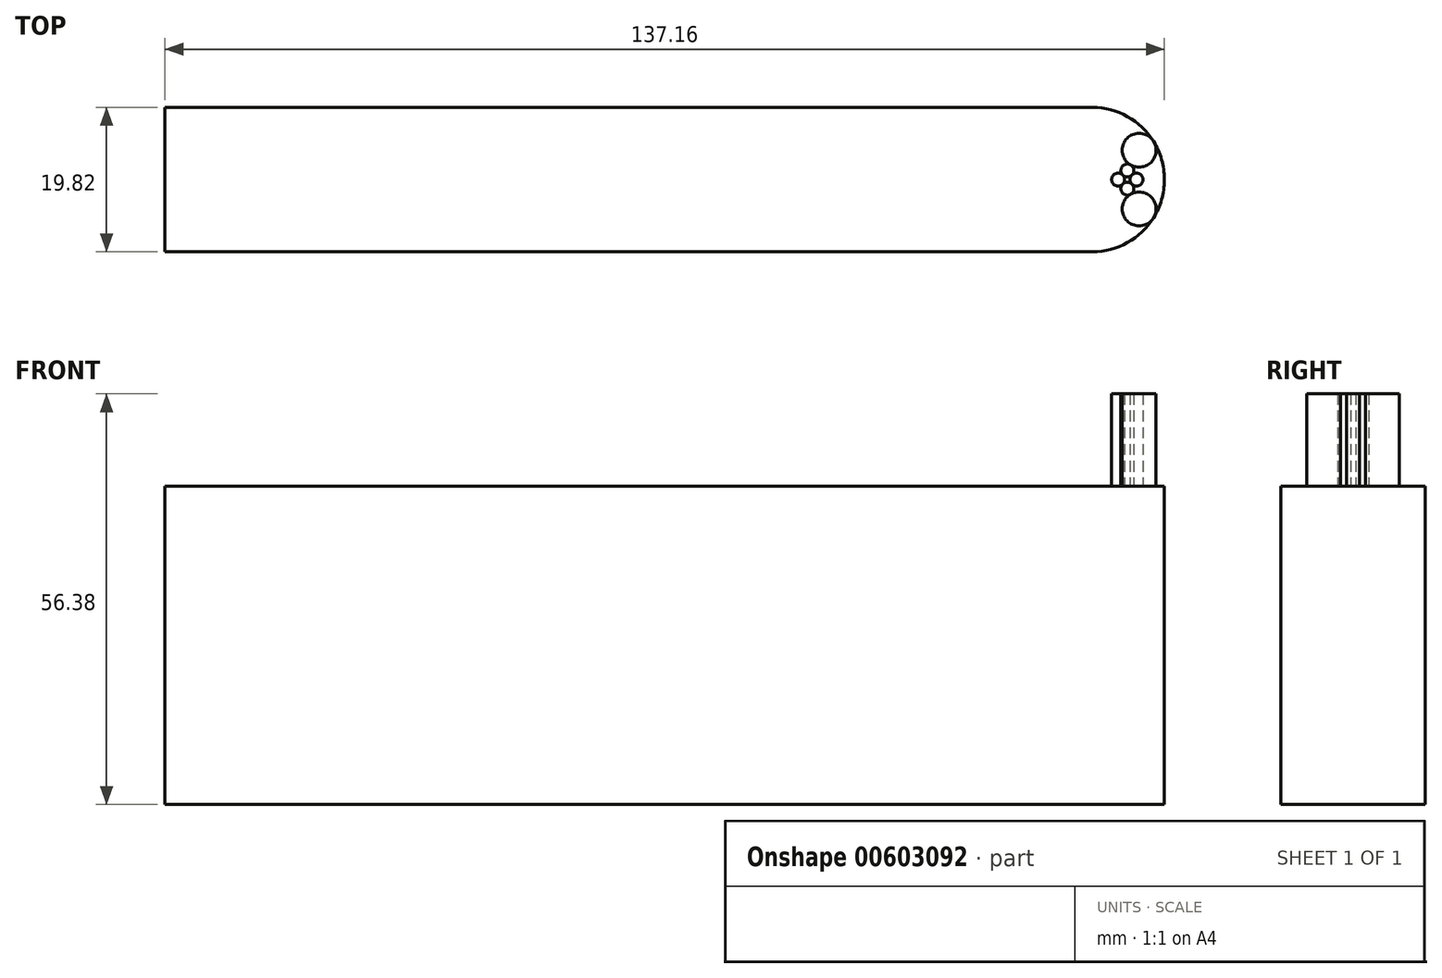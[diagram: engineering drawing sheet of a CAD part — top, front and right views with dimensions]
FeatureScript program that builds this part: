
annotation { "Feature Type Name" : "Feature", "Feature Type Description" : "" }
export const myFeature = defineFeature(function(context is Context, id is Id, definition is map)
    precondition{}
    {
        {
            var Q0;
            Q0=qCreatedBy(makeId("Front.planeOp"),FACE);
            var sketch = newSketch(context, id + "F0", { "sketchPlane" : qUnion([Q0])});
            skLineSegment(sketch, "E0.bottom", {"start": v(68.58, 21.84) * mm, "end": v(-68.58, 21.84) * mm});
            skLineSegment(sketch, "E0.top", {"start": v(68.58, -21.84) * mm, "end": v(-68.58, -21.84) * mm});
            skLineSegment(sketch, "E0.left", {"start": v(68.58, 21.84) * mm, "end": v(68.58, -21.84) * mm});
            skLineSegment(sketch, "E0.right", {"start": v(-68.58, 21.84) * mm, "end": v(-68.58, -21.84) * mm});
            skPoint(sketch, "E0.middle", {"position": v(0, 0) * mm});
            skSolve(sketch);
        }
        {
            var Q0;
            Q0 = qSketchRegion(id + "F0", true);
            extrude(context, id + "F1", {"entities" : qUnion([Q0]), "endBound" : BoundingType.SYMMETRIC, "depth" : 19.8 * mm, "offsetDistance" : 25.4 * mm});
        }
        {
            var Q0;
            Q0=makeQuery(id+"F1.opExtrude","CAP_EDGE",EDGE,{"disambiguationData":[OSD([sQuery(id+"F0.wireOp",EDGE,"E0.left")])],"isStart":false});
            var Q1;
            Q1=makeQuery(id+"F1.opExtrude","CAP_EDGE",EDGE,{"disambiguationData":[OSD([sQuery(id+"F0.wireOp",EDGE,"E0.left")])],"isStart":true});
            fillet(context, id + "F2", {"entities" : qUnion([Q0, Q1]), "radius" : 9.86 * mm, "tangentPropagation" : true, "allowEdgeOverflow" : false});
        }
        {
            var Q0;
            Q0=makeQuery(id+"F1.opExtrude","SWEPT_FACE",FACE,{"disambiguationData":[OSD([sQuery(id+"F0.wireOp",EDGE,"E0.bottom")])]});
            var sketch = newSketch(context, id + "F3", { "sketchPlane" : qUnion([Q0])});
            skCircle(sketch, "E1", {"center": v(65.12, 4.03) * mm, "radius": 2.32 * mm});
            skCircle(sketch, "E2", {"center": v(65.12, -4.03) * mm, "radius": 2.32 * mm});
            skCircle(sketch, "E3", {"center": v(64.77, 0) * mm, "radius": 0.89 * mm});
            skCircle(sketch, "E4", {"center": v(63.5, -1.25) * mm, "radius": 0.89 * mm});
            skCircle(sketch, "E5", {"center": v(63.5, 1.25) * mm, "radius": 0.89 * mm});
            skCircle(sketch, "E6", {"center": v(62.24, 0) * mm, "radius": 0.89 * mm});
            skSolve(sketch);
        }
        {
            var Q0;
            {var subQ0=sQuery(id+"F3.wireOp",EDGE,"E5");var subQ1=makeQuery(id+"F3.imprint","INTERSECT",VERTEX,{"derivedFrom":[sQuery(id+"F3.wireOp",EDGE,"E1"),subQ0]});Q0=makeQuery(id+"F3.imprint","IMPRINT",FACE,{"disambiguationData":[TD([[makeQuery(id+"F3.imprint","IMPRINT",EDGE,{"disambiguationData":[TD([[subQ1,-1.0]])],"derivedFrom":subQ0}),1.0]])]});}
            var Q1;
            {var subQ0=sQuery(id+"F3.wireOp",EDGE,"E6");var subQ1=makeQuery(id+"F3.imprint","INTERSECT",VERTEX,{"derivedFrom":[sQuery(id+"F3.wireOp",EDGE,"E4"),subQ0]});Q1=makeQuery(id+"F3.imprint","IMPRINT",FACE,{"disambiguationData":[TD([[makeQuery(id+"F3.imprint","IMPRINT",EDGE,{"disambiguationData":[TD([[subQ1,1.0]])],"derivedFrom":subQ0}),1.0]])]});}
            var Q2;
            {var subQ0=sQuery(id+"F3.wireOp",EDGE,"E4");var subQ1=makeQuery(id+"F3.imprint","INTERSECT",VERTEX,{"derivedFrom":[sQuery(id+"F3.wireOp",EDGE,"E3"),subQ0]});Q2=makeQuery(id+"F3.imprint","IMPRINT",FACE,{"disambiguationData":[TD([[makeQuery(id+"F3.imprint","IMPRINT",EDGE,{"disambiguationData":[TD([[subQ1,-1.0]])],"derivedFrom":subQ0}),1.0]])]});}
            var Q3;
            {var subQ0=sQuery(id+"F3.wireOp",EDGE,"E3");var subQ1=makeQuery(id+"F3.imprint","INTERSECT",VERTEX,{"derivedFrom":[subQ0,sQuery(id+"F3.wireOp",EDGE,"E4")]});Q3=makeQuery(id+"F3.imprint","IMPRINT",FACE,{"disambiguationData":[TD([[makeQuery(id+"F3.imprint","IMPRINT",EDGE,{"disambiguationData":[TD([[subQ1,1.0]])],"derivedFrom":subQ0}),1.0]])]});}
            var Q4;
            {var subQ0=sQuery(id+"F3.wireOp",EDGE,"E1");var subQ1=makeQuery(id+"F3.imprint","INTERSECT",VERTEX,{"derivedFrom":[subQ0,sQuery(id+"F3.wireOp",EDGE,"E5")]});Q4=makeQuery(id+"F3.imprint","IMPRINT",FACE,{"disambiguationData":[TD([[makeQuery(id+"F3.imprint","IMPRINT",EDGE,{"disambiguationData":[TD([[subQ1,1.0]])],"derivedFrom":subQ0}),1.0]])]});}
            var Q5;
            {var subQ0=sQuery(id+"F3.wireOp",EDGE,"E2");var subQ1=makeQuery(id+"F3.imprint","INTERSECT",VERTEX,{"derivedFrom":[subQ0,sQuery(id+"F3.wireOp",EDGE,"E4")]});Q5=makeQuery(id+"F3.imprint","IMPRINT",FACE,{"disambiguationData":[TD([[makeQuery(id+"F3.imprint","IMPRINT",EDGE,{"disambiguationData":[TD([[subQ1,-1.0]])],"derivedFrom":subQ0}),1.0]])]});}
            extrude(context, id + "F4", {"entities" : qUnion([Q0, Q1, Q2, Q3, Q4, Q5]), "depth" : 12.7 * mm, "offsetDistance" : 25.4 * mm});
        }
    });
